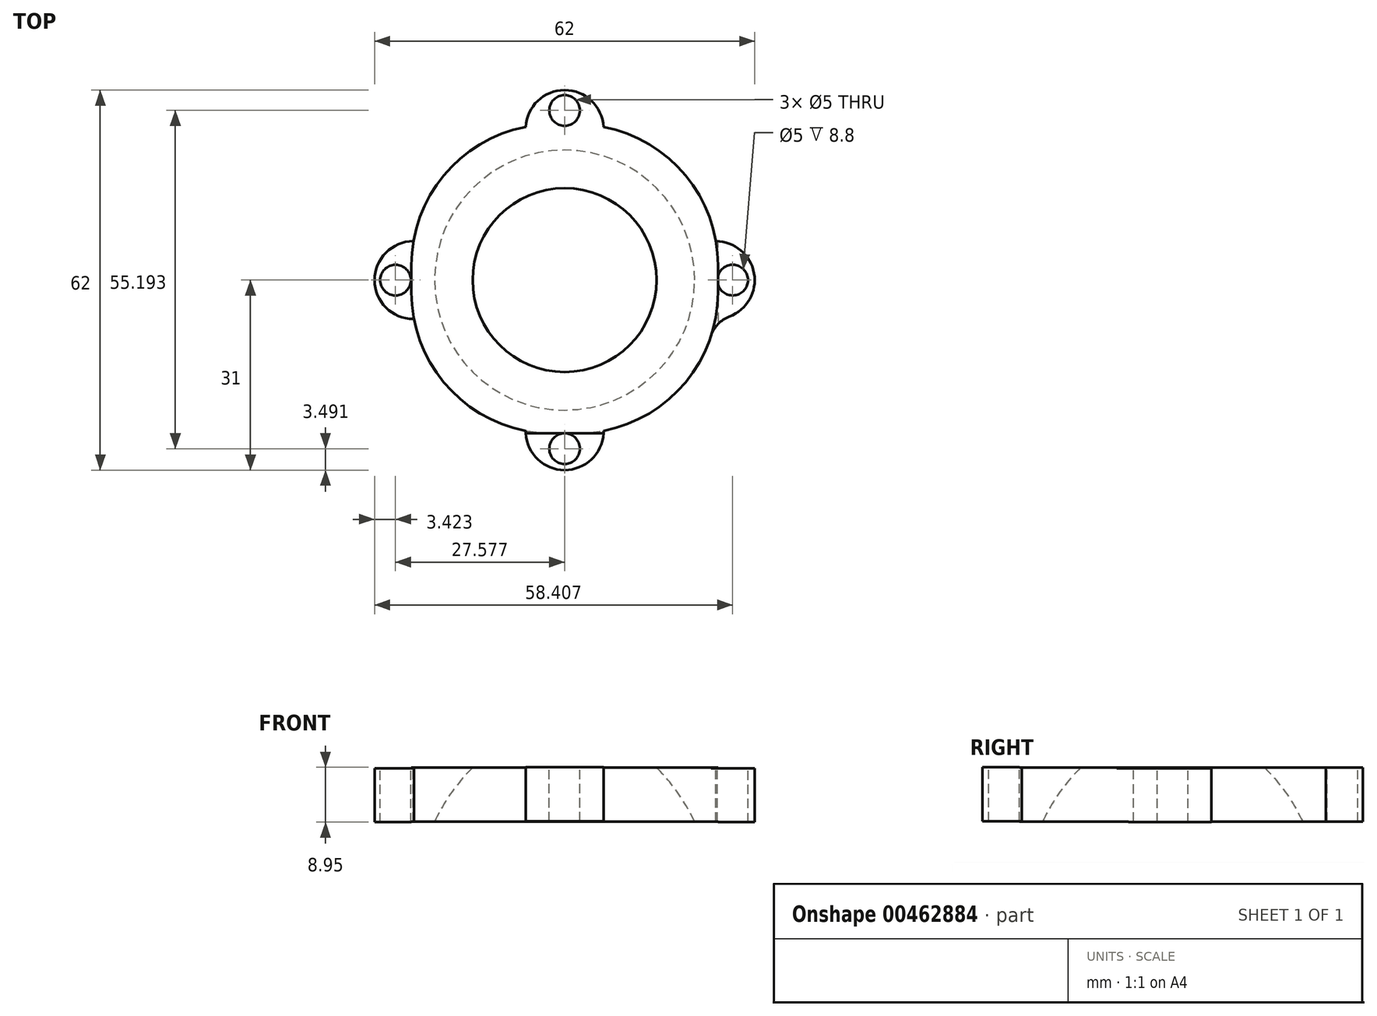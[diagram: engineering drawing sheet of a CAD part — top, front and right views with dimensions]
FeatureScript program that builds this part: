
annotation { "Feature Type Name" : "Feature", "Feature Type Description" : "" }
export const myFeature = defineFeature(function(context is Context, id is Id, definition is map)
    precondition{}
    {
        {
            var Q0;
            Q0=qCreatedBy(makeId("Front.planeOp"),FACE);
            var sketch = newSketch(context, id + "F0", { "sketchPlane" : qUnion([Q0])});
            skEllipticalArc(sketch, "E0", {});
            skLineSegment(sketch, "E1", {"start": v(0, 0) * mm, "end": v(0, 32.5) * mm});
            skLineSegment(sketch, "E2", {"start": v(0, 32.5) * mm, "end": v(0, -32.5) * mm});
            skLineSegment(sketch, "E3", {"start": v(0, 0) * mm, "end": v(25, 0) * mm});
            const initialGuessF0  = {"E0": [0, 0, 0, -1, 0.0325, 0.025, 0, 3.141592653589793]};
            skSetInitialGuess(sketch, initialGuessF0);
            skSolve(sketch);
        }
        {
            var Q0;
            {var subQ0=sQuery(id+"F0.wireOp",EDGE,"E0");Q0=makeQuery(id+"F0.imprint","IMPRINT",FACE,{"disambiguationData":[TD([[makeQuery(id+"F0.imprint","IMPRINT",EDGE,{"derivedFrom":subQ0}),1.0]])]});}
            var Q1;
            Q1=sQuery(id+"F0.wireOp",EDGE,"E2");
            revolve(context, id + "F1", {"entities" : qUnion([Q0]), "axis" : qUnion([Q1]), "revolveType" : RevolveType.FULL});
        }
        {
            var Q0;
            Q0=qCreatedBy(makeId("Top.planeOp"),FACE);
            cPlane(context, id + "F2", {"entities" : qUnion([Q0]), "cplaneType" : CPlaneType.OFFSET, "offset" : 17.2 * mm, "width" : 152.4 * mm, "height" : 152.4 * mm});
        }
        {
            var Q0;
            Q0=qCreatedBy(id+"F2.planeOp",FACE);
            var sketch = newSketch(context, id + "F3", { "sketchPlane" : qUnion([Q0])});
            skLineSegment(sketch, "E4.bottom", {"start": v(25, -25) * mm, "end": v(-25, -25) * mm});
            skLineSegment(sketch, "E4.top", {"start": v(25, 25) * mm, "end": v(-25, 25) * mm});
            skLineSegment(sketch, "E4.left", {"start": v(25, -25) * mm, "end": v(25, 25) * mm});
            skLineSegment(sketch, "E4.right", {"start": v(-25, -25) * mm, "end": v(-25, 25) * mm});
            skPoint(sketch, "E4.middle", {"position": v(0, 0) * mm});
            skSolve(sketch);
        }
        {
            var Q0;
            Q0=qSketchRegion(id+"F3",true);
            extrude(context, id + "F4", {"entities" : qUnion([Q0]), "depth" : 8.8 * mm});
        }
        {
            var Q0;
            Q0=makeQuery(id+"F1.opRevolve","SWEPT_BODY",BODY,{"disambiguationData":[OSD([sQuery(id+"F0.wireOp",EDGE,"E0"),sQuery(id+"F0.wireOp",EDGE,"E2")])]});
            var Q1;
            Q1=makeQuery(id+"F4.opExtrude","SWEPT_BODY",BODY,{"disambiguationData":[OSD([sQuery(id+"F3.wireOp",EDGE,"E4.bottom"),sQuery(id+"F3.wireOp",EDGE,"E4.top"),sQuery(id+"F3.wireOp",EDGE,"E4.left"),sQuery(id+"F3.wireOp",EDGE,"E4.right")])]});
            booleanBodies(context, id + "F5", {"operationType" : BooleanOperationType.SUBTRACTION, "tools" : qUnion([Q0]), "targets" : qUnion([Q1])});
        }
        {
            var Q0;
            Q0=qCreatedBy(makeId("Front.planeOp"),FACE);
            var Q1;
            Q1=qBodyType(qCreatedBy(id+"F7",EDGE),BodyType.WIRE);
            cPlane(context, id + "F6", {"entities" : qUnion([Q0, Q1]), "cplaneType" : CPlaneType.OFFSET, "offset" : 25 * mm, "width" : 152.4 * mm, "height" : 152.4 * mm});
        }
        {
            var Q0;
            Q0=qCreatedBy(id+"F6.planeOp",FACE);
            var sketch = newSketch(context, id + "F7", { "sketchPlane" : qUnion([Q0])});
            skLineSegment(sketch, "E5.bottom", {"start": v(6.35, 17.26) * mm, "end": v(-6.35, 17.26) * mm});
            skLineSegment(sketch, "E5.top", {"start": v(6.35, 26.06) * mm, "end": v(-6.35, 26.06) * mm});
            skLineSegment(sketch, "E5.left", {"start": v(6.35, 17.26) * mm, "end": v(6.35, 26.06) * mm});
            skLineSegment(sketch, "E5.right", {"start": v(-6.35, 17.26) * mm, "end": v(-6.35, 26.06) * mm});
            skPoint(sketch, "E5.middle", {"position": v(0, 21.66) * mm});
            skSolve(sketch);
        }
        {
            var Q0;
            Q0=makeQuery(id+"F7.imprint","IMPRINT",FACE,{"disambiguationData":[TD([[makeQuery(id+"F7.imprint","IMPRINT",EDGE,{"derivedFrom":sQuery(id+"F7.wireOp",EDGE,"E5.bottom")}),-1.0]])]});
            extrude(context, id + "F8", {"entities" : qUnion([Q0]), "operationType" : NewBodyOperationType.ADD, "depth" : 6 * mm});
        }
        {
            var Q0;
            Q0=qCreatedBy(makeId("Right.planeOp"),FACE);
            cPlane(context, id + "F9", {"entities" : qUnion([Q0]), "cplaneType" : CPlaneType.OFFSET, "offset" : 25 * mm, "width" : 152.4 * mm, "height" : 152.4 * mm});
        }
        {
            var Q0;
            Q0=qCreatedBy(id+"F9.planeOp",FACE);
            var sketch = newSketch(context, id + "F10", { "sketchPlane" : qUnion([Q0])});
            skLineSegment(sketch, "E6.bottom", {"start": v(6.35, 17.12) * mm, "end": v(-6.35, 17.12) * mm});
            skLineSegment(sketch, "E6.top", {"start": v(6.35, 25.92) * mm, "end": v(-6.35, 25.92) * mm});
            skLineSegment(sketch, "E6.left", {"start": v(6.35, 17.12) * mm, "end": v(6.35, 25.92) * mm});
            skLineSegment(sketch, "E6.right", {"start": v(-6.35, 17.12) * mm, "end": v(-6.35, 25.92) * mm});
            skPoint(sketch, "E6.middle", {"position": v(0, 21.52) * mm});
            skSolve(sketch);
        }
        {
            var Q0;
            Q0=makeQuery(id+"F10.imprint","IMPRINT",FACE,{"disambiguationData":[TD([[makeQuery(id+"F10.imprint","IMPRINT",EDGE,{"derivedFrom":sQuery(id+"F10.wireOp",EDGE,"E6.bottom")}),-1.0]])]});
            extrude(context, id + "F11", {"entities" : qUnion([Q0]), "operationType" : NewBodyOperationType.ADD, "depth" : 6 * mm});
        }
        {
            var Q0;
            Q0=qCreatedBy(makeId("Front.planeOp"),FACE);
            cPlane(context, id + "F12", {"entities" : qUnion([Q0]), "cplaneType" : CPlaneType.OFFSET, "offset" : 25 * mm, "oppositeDirection" : true, "width" : 152.4 * mm, "height" : 152.4 * mm});
        }
        {
            var Q0;
            Q0=qCreatedBy(id+"F12.planeOp",FACE);
            var sketch = newSketch(context, id + "F13", { "sketchPlane" : qUnion([Q0])});
            skLineSegment(sketch, "E7.bottom", {"start": v(6.35, 17.2) * mm, "end": v(-6.35, 17.2) * mm});
            skLineSegment(sketch, "E7.top", {"start": v(6.35, 26) * mm, "end": v(-6.35, 26) * mm});
            skLineSegment(sketch, "E7.left", {"start": v(6.35, 17.2) * mm, "end": v(6.35, 26) * mm});
            skLineSegment(sketch, "E7.right", {"start": v(-6.35, 17.2) * mm, "end": v(-6.35, 26) * mm});
            skPoint(sketch, "E7.middle", {"position": v(0, 21.6) * mm});
            skSolve(sketch);
        }
        {
            var Q0;
            Q0=makeQuery(id+"F13.imprint","IMPRINT",FACE,{"disambiguationData":[TD([[makeQuery(id+"F13.imprint","IMPRINT",EDGE,{"derivedFrom":sQuery(id+"F13.wireOp",EDGE,"E7.bottom")}),-1.0]])]});
            extrude(context, id + "F14", {"entities" : qUnion([Q0]), "operationType" : NewBodyOperationType.ADD, "oppositeDirection" : true, "depth" : 6 * mm});
        }
        {
            var Q0;
            Q0=qCreatedBy(makeId("Right.planeOp"),FACE);
            cPlane(context, id + "F15", {"entities" : qUnion([Q0]), "cplaneType" : CPlaneType.OFFSET, "offset" : 25 * mm, "oppositeDirection" : true, "width" : 152.4 * mm, "height" : 152.4 * mm});
        }
        {
            var Q0;
            Q0=qCreatedBy(id+"F15.planeOp",FACE);
            var sketch = newSketch(context, id + "F16", { "sketchPlane" : qUnion([Q0])});
            skLineSegment(sketch, "E8.bottom", {"start": v(-6.35, 17.11) * mm, "end": v(6.35, 17.11) * mm});
            skLineSegment(sketch, "E8.top", {"start": v(-6.35, 25.91) * mm, "end": v(6.35, 25.91) * mm});
            skLineSegment(sketch, "E8.left", {"start": v(-6.35, 17.11) * mm, "end": v(-6.35, 25.91) * mm});
            skLineSegment(sketch, "E8.right", {"start": v(6.35, 17.11) * mm, "end": v(6.35, 25.91) * mm});
            skPoint(sketch, "E8.middle", {"position": v(0, 21.51) * mm});
            skSolve(sketch);
        }
        {
            var Q0;
            Q0=makeQuery(id+"F16.imprint","IMPRINT",FACE,{"disambiguationData":[TD([[makeQuery(id+"F16.imprint","IMPRINT",EDGE,{"derivedFrom":sQuery(id+"F16.wireOp",EDGE,"E8.bottom")}),1.0]])]});
            extrude(context, id + "F17", {"entities" : qUnion([Q0]), "operationType" : NewBodyOperationType.ADD, "oppositeDirection" : true, "depth" : 6 * mm});
        }
        {
            var Q0;
            Q0=makeQuery(id+"F14.opExtrude","SWEPT_FACE",FACE,{"disambiguationData":[OSD([sQuery(id+"F13.wireOp",EDGE,"E7.top")])]});
            var sketch = newSketch(context, id + "F18", { "sketchPlane" : qUnion([Q0])});
            skLineSegment(sketch, "E9", {"start": v(0, 35.08) * mm, "end": v(0, 20.28) * mm});
            skPoint(sketch, "E9.endSnap0", {"position": v(0, 25) * mm});
            skPoint(sketch, "E10", {"position": v(0, 27.68) * mm});
            skSolve(sketch);
        }
        {
            var Q0;
            Q0=sQuery(id+"F18.wireOp",VERTEX,"E10");
            var Q1;
            Q1=makeQuery(id+"F4.opExtrude","SWEPT_BODY",BODY,{"disambiguationData":[OSD([sQuery(id+"F3.wireOp",EDGE,"E4.bottom"),sQuery(id+"F3.wireOp",EDGE,"E4.top"),sQuery(id+"F3.wireOp",EDGE,"E4.left"),sQuery(id+"F3.wireOp",EDGE,"E4.right")])]});
            hole(context, id + "F19", {"style" : HoleStyle.SIMPLE, "endStyle" : HoleEndStyle.THROUGH, "holeDiameter" : 5 * mm, "isTappedThrough" : true, "tappedDepth" : 12.7 * mm, "tapClearance" : 3, "locations" : qUnion([Q0]), "scope" : qUnion([Q1])});
        }
        {
            var Q0;
            Q0=makeQuery(id+"F17.opExtrude","SWEPT_FACE",FACE,{"disambiguationData":[OSD([sQuery(id+"F16.wireOp",EDGE,"E8.top")])]});
            var sketch = newSketch(context, id + "F20", { "sketchPlane" : qUnion([Q0])});
            skLineSegment(sketch, "E11", {"start": v(-37.5, 0) * mm, "end": v(-17.65, 0) * mm});
            skPoint(sketch, "E12", {"position": v(-27.58, 0) * mm});
            skSolve(sketch);
        }
        {
            var Q0;
            Q0=sQuery(id+"F20.wireOp",VERTEX,"E12");
            var Q1;
            Q1=makeQuery(id+"F4.opExtrude","SWEPT_BODY",BODY,{"disambiguationData":[OSD([sQuery(id+"F3.wireOp",EDGE,"E4.bottom"),sQuery(id+"F3.wireOp",EDGE,"E4.top"),sQuery(id+"F3.wireOp",EDGE,"E4.left"),sQuery(id+"F3.wireOp",EDGE,"E4.right")])]});
            hole(context, id + "F21", {"style" : HoleStyle.SIMPLE, "endStyle" : HoleEndStyle.THROUGH, "holeDiameter" : 5 * mm, "isTappedThrough" : true, "tappedDepth" : 12.7 * mm, "tapClearance" : 3, "locations" : qUnion([Q0]), "scope" : qUnion([Q1])});
        }
        {
            var Q0;
            Q0=makeQuery(id+"F11.opExtrude","SWEPT_FACE",FACE,{"disambiguationData":[OSD([sQuery(id+"F10.wireOp",EDGE,"E6.top")])]});
            var sketch = newSketch(context, id + "F22", { "sketchPlane" : qUnion([Q0])});
            skLineSegment(sketch, "E13", {"start": v(34.55, 0) * mm, "end": v(20.26, 0) * mm});
            skPoint(sketch, "E13.endSnap0", {"position": v(25, 0) * mm});
            skPoint(sketch, "E14", {"position": v(27.4, 0) * mm});
            skSolve(sketch);
        }
        {
            var Q0;
            Q0=sQuery(id+"F22.wireOp",VERTEX,"E14");
            var Q1;
            Q1=makeQuery(id+"F4.opExtrude","SWEPT_BODY",BODY,{"disambiguationData":[OSD([sQuery(id+"F3.wireOp",EDGE,"E4.bottom"),sQuery(id+"F3.wireOp",EDGE,"E4.top"),sQuery(id+"F3.wireOp",EDGE,"E4.left"),sQuery(id+"F3.wireOp",EDGE,"E4.right")])]});
            hole(context, id + "F23", {"style" : HoleStyle.SIMPLE, "endStyle" : HoleEndStyle.THROUGH, "holeDiameter" : 5 * mm, "isTappedThrough" : true, "tappedDepth" : 12.7 * mm, "tapClearance" : 3, "locations" : qUnion([Q0]), "scope" : qUnion([Q1])});
        }
        {
            var Q0;
            Q0=makeQuery(id+"F8.opExtrude","SWEPT_FACE",FACE,{"disambiguationData":[OSD([sQuery(id+"F7.wireOp",EDGE,"E5.top")])]});
            var sketch = newSketch(context, id + "F24", { "sketchPlane" : qUnion([Q0])});
            skLineSegment(sketch, "E15", {"start": v(0, -34.8) * mm, "end": v(0, -20.22) * mm});
            skPoint(sketch, "E15.endSnap0", {"position": v(0, -25) * mm});
            skPoint(sketch, "E16", {"position": v(0, -27.5) * mm});
            skSolve(sketch);
        }
        {
            var Q0;
            Q0=sQuery(id+"F24.wireOp",VERTEX,"E16");
            var Q1;
            Q1=makeQuery(id+"F4.opExtrude","SWEPT_BODY",BODY,{"disambiguationData":[OSD([sQuery(id+"F3.wireOp",EDGE,"E4.bottom"),sQuery(id+"F3.wireOp",EDGE,"E4.top"),sQuery(id+"F3.wireOp",EDGE,"E4.left"),sQuery(id+"F3.wireOp",EDGE,"E4.right")])]});
            hole(context, id + "F25", {"style" : HoleStyle.SIMPLE, "endStyle" : HoleEndStyle.THROUGH, "holeDiameter" : 5 * mm, "isTappedThrough" : true, "tappedDepth" : 12.7 * mm, "tapClearance" : 3, "locations" : qUnion([Q0]), "scope" : qUnion([Q1])});
        }
        {
            var Q0;
            Q0=makeQuery(id+"F4.opExtrude","SWEPT_EDGE",EDGE,{"disambiguationData":[OSD([sQuery(id+"F3.wireOp",EDGE,"E4.bottom"),sQuery(id+"F3.wireOp",EDGE,"E4.left")])]});
            var Q1;
            Q1=makeQuery(id+"F4.opExtrude","SWEPT_EDGE",EDGE,{"disambiguationData":[OSD([sQuery(id+"F3.wireOp",EDGE,"E4.bottom"),sQuery(id+"F3.wireOp",EDGE,"E4.right")])]});
            var Q2;
            Q2=makeQuery(id+"F4.opExtrude","SWEPT_EDGE",EDGE,{"disambiguationData":[OSD([sQuery(id+"F3.wireOp",EDGE,"E4.top"),sQuery(id+"F3.wireOp",EDGE,"E4.left")])]});
            var Q3;
            Q3=makeQuery(id+"F4.opExtrude","SWEPT_EDGE",EDGE,{"disambiguationData":[OSD([sQuery(id+"F3.wireOp",EDGE,"E4.top"),sQuery(id+"F3.wireOp",EDGE,"E4.right")])]});
            fillet(context, id + "F26", {"entities" : qUnion([Q0, Q1, Q2, Q3]), "radius" : 23 * mm, "tangentPropagation" : true, "allowEdgeOverflow" : false});
        }
        {
            var Q0;
            Q0=makeQuery(id+"F14.opExtrude","CAP_EDGE",EDGE,{"disambiguationData":[OSD([sQuery(id+"F13.wireOp",EDGE,"E7.left")])],"isStart":false});
            var Q1;
            Q1=makeQuery(id+"F14.opExtrude","CAP_EDGE",EDGE,{"disambiguationData":[OSD([sQuery(id+"F13.wireOp",EDGE,"E7.right")])],"isStart":false});
            var Q2;
            Q2=makeQuery(id+"F17.opExtrude","CAP_EDGE",EDGE,{"disambiguationData":[OSD([sQuery(id+"F16.wireOp",EDGE,"E8.right")])],"isStart":false});
            var Q3;
            Q3=makeQuery(id+"F17.opExtrude","CAP_EDGE",EDGE,{"disambiguationData":[OSD([sQuery(id+"F16.wireOp",EDGE,"E8.left")])],"isStart":false});
            var Q4;
            Q4=makeQuery(id+"F8.opExtrude","CAP_EDGE",EDGE,{"disambiguationData":[OSD([sQuery(id+"F7.wireOp",EDGE,"E5.right")])],"isStart":false});
            var Q5;
            Q5=makeQuery(id+"F8.opExtrude","CAP_EDGE",EDGE,{"disambiguationData":[OSD([sQuery(id+"F7.wireOp",EDGE,"E5.left")])],"isStart":false});
            var Q6;
            Q6=makeQuery(id+"F11.opExtrude","CAP_EDGE",EDGE,{"disambiguationData":[OSD([sQuery(id+"F10.wireOp",EDGE,"E6.right")])],"isStart":false});
            var Q7;
            Q7=makeQuery(id+"F11.opExtrude","CAP_EDGE",EDGE,{"disambiguationData":[OSD([sQuery(id+"F10.wireOp",EDGE,"E6.left")])],"isStart":false});
            fillet(context, id + "F27", {"entities" : qUnion([Q0, Q1, Q2, Q3, Q4, Q5, Q6, Q7]), "radius" : 6.35 * mm, "tangentPropagation" : true, "allowEdgeOverflow" : false});
        }
        {
            var Q0;
            Q0=makeQuery(id+"F26.opFillet","BLEND_EDGE",EDGE,{"blendedFrom":[makeQuery(id+"F4.opExtrude","SWEPT_EDGE",EDGE,{"disambiguationData":[OSD([sQuery(id+"F3.wireOp",EDGE,"E4.top"),sQuery(id+"F3.wireOp",EDGE,"E4.left")])]}),makeQuery(id+"F14.opExtrude","SWEPT_FACE",FACE,{"disambiguationData":[OSD([sQuery(id+"F13.wireOp",EDGE,"E7.left")])]})],"blendedInto":[makeQuery(id+"F14.opExtrude","SWEPT_FACE",FACE,{"disambiguationData":[OSD([sQuery(id+"F13.wireOp",EDGE,"E7.left")])]})]});
            var Q1;
            Q1=makeQuery(id+"F26.opFillet","BLEND_EDGE",EDGE,{"blendedFrom":[makeQuery(id+"F4.opExtrude","SWEPT_EDGE",EDGE,{"disambiguationData":[OSD([sQuery(id+"F3.wireOp",EDGE,"E4.top"),sQuery(id+"F3.wireOp",EDGE,"E4.left")])]}),makeQuery(id+"F11.opExtrude","SWEPT_FACE",FACE,{"disambiguationData":[OSD([sQuery(id+"F10.wireOp",EDGE,"E6.left")])]})],"blendedInto":[makeQuery(id+"F11.opExtrude","SWEPT_FACE",FACE,{"disambiguationData":[OSD([sQuery(id+"F10.wireOp",EDGE,"E6.left")])]})]});
            var Q2;
            Q2=makeQuery(id+"F26.opFillet","BLEND_EDGE",EDGE,{"blendedFrom":[makeQuery(id+"F4.opExtrude","SWEPT_EDGE",EDGE,{"disambiguationData":[OSD([sQuery(id+"F3.wireOp",EDGE,"E4.bottom"),sQuery(id+"F3.wireOp",EDGE,"E4.left")])]}),makeQuery(id+"F11.opExtrude","SWEPT_FACE",FACE,{"disambiguationData":[OSD([sQuery(id+"F10.wireOp",EDGE,"E6.right")])]})],"blendedInto":[makeQuery(id+"F11.opExtrude","SWEPT_FACE",FACE,{"disambiguationData":[OSD([sQuery(id+"F10.wireOp",EDGE,"E6.right")])]})]});
            var Q3;
            Q3=makeQuery(id+"F26.opFillet","BLEND_EDGE",EDGE,{"blendedFrom":[makeQuery(id+"F4.opExtrude","SWEPT_EDGE",EDGE,{"disambiguationData":[OSD([sQuery(id+"F3.wireOp",EDGE,"E4.top"),sQuery(id+"F3.wireOp",EDGE,"E4.right")])]}),makeQuery(id+"F17.opExtrude","SWEPT_FACE",FACE,{"disambiguationData":[OSD([sQuery(id+"F16.wireOp",EDGE,"E8.right")])]})],"blendedInto":[makeQuery(id+"F17.opExtrude","SWEPT_FACE",FACE,{"disambiguationData":[OSD([sQuery(id+"F16.wireOp",EDGE,"E8.right")])]})]});
            var Q4;
            {var subQ0=sQuery(id+"F16.wireOp",EDGE,"E8.left");Q4=makeQuery(id+"F27.opFillet","BLEND_EDGE",EDGE,{"blendedFrom":[makeQuery(id+"F17.opExtrude","CAP_EDGE",EDGE,{"disambiguationData":[OSD([subQ0])],"isStart":false}),makeQuery(id+"F17.opExtrude","SWEPT_FACE",FACE,{"disambiguationData":[OSD([subQ0])]})],"blendedInto":[makeQuery(id+"F17.opExtrude","SWEPT_FACE",FACE,{"disambiguationData":[OSD([subQ0])]})]});}
            var Q5;
            {var subQ0=sQuery(id+"F13.wireOp",EDGE,"E7.right");Q5=makeQuery(id+"F27.opFillet","BLEND_EDGE",EDGE,{"blendedFrom":[makeQuery(id+"F14.opExtrude","CAP_EDGE",EDGE,{"disambiguationData":[OSD([subQ0])],"isStart":false}),makeQuery(id+"F14.opExtrude","SWEPT_FACE",FACE,{"disambiguationData":[OSD([subQ0])]})],"blendedInto":[makeQuery(id+"F14.opExtrude","SWEPT_FACE",FACE,{"disambiguationData":[OSD([subQ0])]})]});}
            var Q6;
            {var subQ0=sQuery(id+"F7.wireOp",EDGE,"E5.left");Q6=makeQuery(id+"F27.opFillet","BLEND_EDGE",EDGE,{"blendedFrom":[makeQuery(id+"F8.opExtrude","CAP_EDGE",EDGE,{"disambiguationData":[OSD([subQ0])],"isStart":false}),makeQuery(id+"F8.opExtrude","SWEPT_FACE",FACE,{"disambiguationData":[OSD([subQ0])]})],"blendedInto":[makeQuery(id+"F8.opExtrude","SWEPT_FACE",FACE,{"disambiguationData":[OSD([subQ0])]})]});}
            var Q7;
            {var subQ0=sQuery(id+"F7.wireOp",EDGE,"E5.right");Q7=makeQuery(id+"F27.opFillet","BLEND_EDGE",EDGE,{"blendedFrom":[makeQuery(id+"F8.opExtrude","CAP_EDGE",EDGE,{"disambiguationData":[OSD([subQ0])],"isStart":false}),makeQuery(id+"F8.opExtrude","SWEPT_FACE",FACE,{"disambiguationData":[OSD([subQ0])]})],"blendedInto":[makeQuery(id+"F8.opExtrude","SWEPT_FACE",FACE,{"disambiguationData":[OSD([subQ0])]})]});}
            fillet(context, id + "F28", {"entities" : qUnion([Q0, Q1, Q2, Q3, Q4, Q5, Q6, Q7]), "radius" : 5 * mm, "tangentPropagation" : true, "allowEdgeOverflow" : false});
        }
    });
